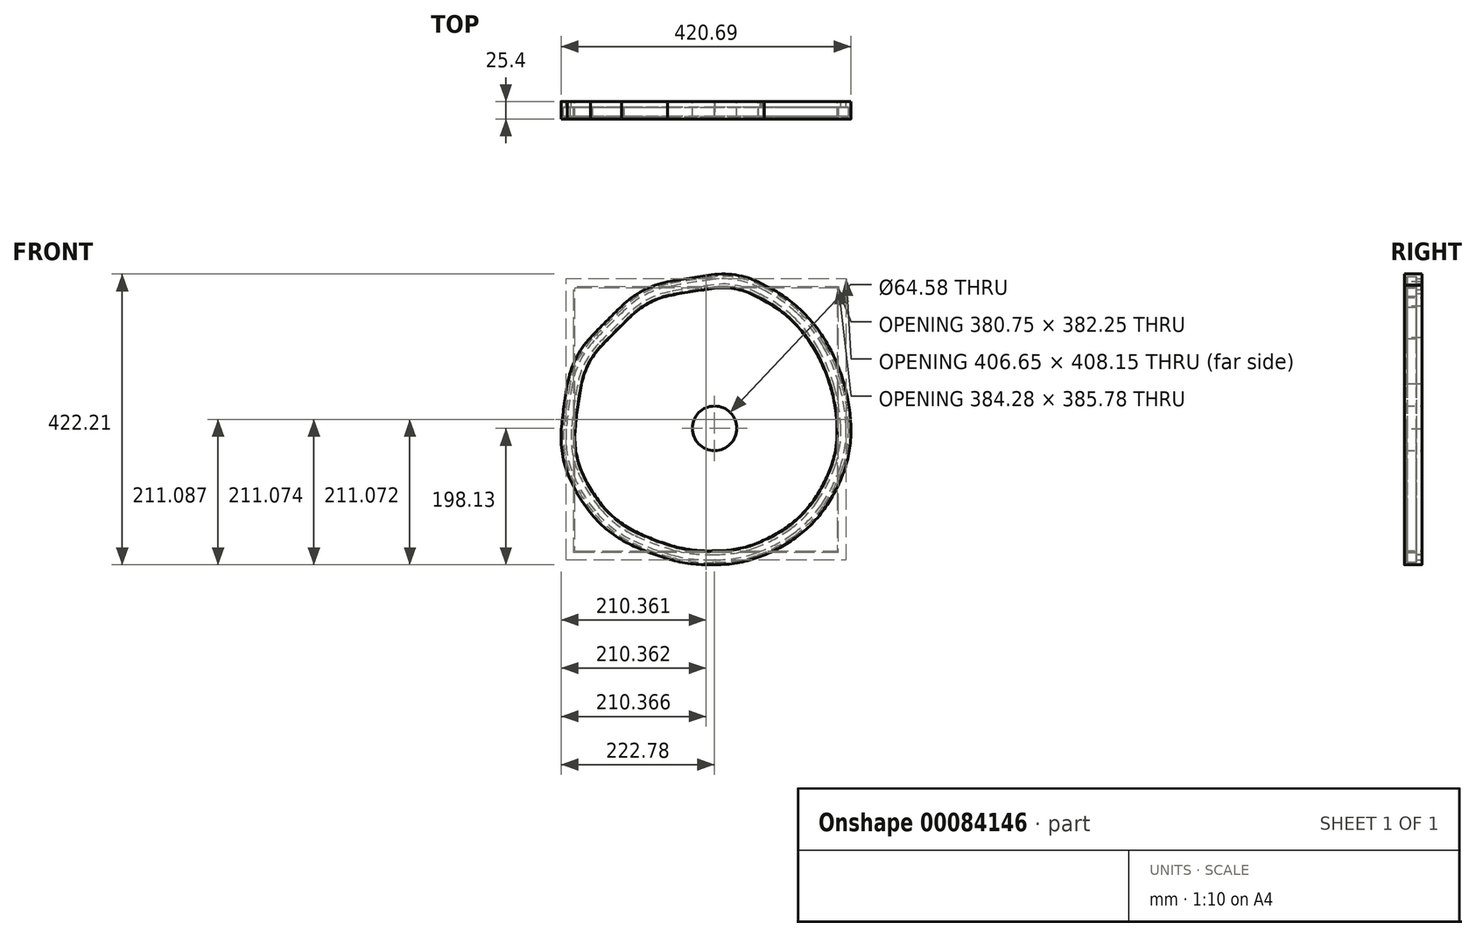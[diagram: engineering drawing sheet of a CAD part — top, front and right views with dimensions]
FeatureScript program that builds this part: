
annotation { "Feature Type Name" : "Feature", "Feature Type Description" : "" }
export const myFeature = defineFeature(function(context is Context, id is Id, definition is map)
    precondition{}
    {
        {
            var Q0;
            Q0=qCreatedBy(makeId("Front.planeOp"),FACE);
            var sketch = newSketch(context, id + "F0", { "sketchPlane" : qUnion([Q0])});
            skPoint(sketch, "E0", {"position": v(0, -177.8) * mm});
            skPoint(sketch, "E1", {"position": v(-58.17, -171.45) * mm});
            skPoint(sketch, "E2", {"position": v(-113.54, -150.62) * mm});
            skPoint(sketch, "E3", {"position": v(-161.3, -113.8) * mm});
            skPoint(sketch, "E4", {"position": v(-193.04, -61.72) * mm});
            skPoint(sketch, "E5", {"position": v(-202.18, -1.27) * mm});
            skPoint(sketch, "E6", {"position": v(-193.3, 62.74) * mm});
            skPoint(sketch, "E7", {"position": v(-164.34, 119.38) * mm});
            skPoint(sketch, "E8", {"position": v(-119.38, 164.34) * mm});
            skPoint(sketch, "E9", {"position": v(-62.74, 193.3) * mm});
            skPoint(sketch, "E10", {"position": v(0, 203.2) * mm});
            skArc(sketch, "E11", {"start": v(-58.17, -171.45) * mm, "mid": v(-29.35, -177.03) * mm, "end": v(0, -177.8) * mm});
            skArc(sketch, "E12", {"start": v(-113.54, -150.62) * mm, "mid": v(-86.3, -162.22) * mm, "end": v(-58.17, -171.45) * mm});
            skArc(sketch, "E13", {"start": v(-161.29, -113.8) * mm, "mid": v(-139.37, -134.74) * mm, "end": v(-113.54, -150.62) * mm});
            skArc(sketch, "E14", {"start": v(-193.04, -61.72) * mm, "mid": v(-179.18, -88.99) * mm, "end": v(-161.3, -113.8) * mm});
            skArc(sketch, "E15", {"start": v(-202.18, -1.27) * mm, "mid": v(-201.3, -32.05) * mm, "end": v(-193.04, -61.72) * mm});
            skArc(sketch, "E16", {"start": v(-193.3, 62.74) * mm, "mid": v(-198.47, 30.84) * mm, "end": v(-202.18, -1.27) * mm});
            skArc(sketch, "E17", {"start": v(-164.34, 119.38) * mm, "mid": v(-182.94, 93.17) * mm, "end": v(-193.3, 62.74) * mm});
            skArc(sketch, "E18", {"start": v(-119.38, 164.34) * mm, "mid": v(-142.13, 142.13) * mm, "end": v(-164.34, 119.38) * mm});
            skArc(sketch, "E19", {"start": v(-62.74, 193.3) * mm, "mid": v(-93.17, 182.94) * mm, "end": v(-119.38, 164.34) * mm});
            skArc(sketch, "E20", {"start": v(0, 203.2) * mm, "mid": v(-31.44, 198.67) * mm, "end": v(-62.74, 193.3) * mm});
            skPoint(sketch, "E21", {"position": v(63, 190) * mm});
            skPoint(sketch, "E22", {"position": v(111.5, 156.97) * mm});
            skPoint(sketch, "E23", {"position": v(147.07, 111) * mm});
            skPoint(sketch, "E24", {"position": v(168.91, 58.17) * mm});
            skPoint(sketch, "E25", {"position": v(177.8, 0) * mm});
            skPoint(sketch, "E26", {"position": v(169.16, -54.86) * mm});
            skPoint(sketch, "E27", {"position": v(143.76, -104.4) * mm});
            skPoint(sketch, "E28", {"position": v(104.4, -143.76) * mm});
            skPoint(sketch, "E29", {"position": v(54.86, -169.16) * mm});
            skArc(sketch, "E30", {"start": v(63, 190) * mm, "mid": v(32.62, 201.94) * mm, "end": v(0, 203.2) * mm});
            skArc(sketch, "E31", {"start": v(111.5, 156.97) * mm, "mid": v(88.62, 175.5) * mm, "end": v(63, 190) * mm});
            skArc(sketch, "E32", {"start": v(147.07, 111) * mm, "mid": v(131, 135.31) * mm, "end": v(111.5, 156.97) * mm});
            skArc(sketch, "E33", {"start": v(168.91, 58.17) * mm, "mid": v(159.54, 85.22) * mm, "end": v(147.07, 111) * mm});
            skArc(sketch, "E34", {"start": v(177.8, 0) * mm, "mid": v(175.15, 29.36) * mm, "end": v(168.9, 58.17) * mm});
            skArc(sketch, "E35", {"start": v(169.16, -54.86) * mm, "mid": v(176.02, -27.83) * mm, "end": v(177.8, 0) * mm});
            skArc(sketch, "E36", {"start": v(143.76, -104.4) * mm, "mid": v(158.11, -80.48) * mm, "end": v(169.16, -54.86) * mm});
            skArc(sketch, "E37", {"start": v(104.4, -143.76) * mm, "mid": v(125.84, -125.84) * mm, "end": v(143.76, -104.4) * mm});
            skArc(sketch, "E38", {"start": v(54.86, -169.16) * mm, "mid": v(80.48, -158.11) * mm, "end": v(104.4, -143.76) * mm});
            skArc(sketch, "E39", {"start": v(0, -177.8) * mm, "mid": v(27.83, -176.02) * mm, "end": v(54.86, -169.16) * mm});
            skCircle(sketch, "E40", {"center": v(0, 0) * mm, "radius": 32.3 * mm});
            skSolve(sketch);
        }
        {
            var Q0;
            Q0 = qSketchRegion(id + "F0", true);
            extrude(context, id + "F1", {"entities" : qUnion([Q0]), "depth" : 25.4 * mm});
        }
        {
            var Q0;
            Q0=makeQuery(id+"F1.opExtrude","CAP_FACE",FACE,{"disambiguationData":[OSD([sQuery(id+"F0.wireOp",EDGE,"E11"),sQuery(id+"F0.wireOp",EDGE,"E12"),sQuery(id+"F0.wireOp",EDGE,"E13"),sQuery(id+"F0.wireOp",EDGE,"E14"),sQuery(id+"F0.wireOp",EDGE,"E15"),sQuery(id+"F0.wireOp",EDGE,"E16"),sQuery(id+"F0.wireOp",EDGE,"E17"),sQuery(id+"F0.wireOp",EDGE,"E18"),sQuery(id+"F0.wireOp",EDGE,"E19"),sQuery(id+"F0.wireOp",EDGE,"E20"),sQuery(id+"F0.wireOp",EDGE,"E30"),sQuery(id+"F0.wireOp",EDGE,"E31"),sQuery(id+"F0.wireOp",EDGE,"E32"),sQuery(id+"F0.wireOp",EDGE,"E33"),sQuery(id+"F0.wireOp",EDGE,"E34"),sQuery(id+"F0.wireOp",EDGE,"E35"),sQuery(id+"F0.wireOp",EDGE,"E36"),sQuery(id+"F0.wireOp",EDGE,"E37"),sQuery(id+"F0.wireOp",EDGE,"E38"),sQuery(id+"F0.wireOp",EDGE,"E39"),sQuery(id+"F0.wireOp",EDGE,"E40")])],"isStart":true});
            var sketch = newSketch(context, id + "F2", { "sketchPlane" : qUnion([Q0])});
            skArc(sketch, "E41.0.0", {"start": v(58.17, -171.45) * mm, "mid": v(86.3, -162.22) * mm, "end": v(113.54, -150.62) * mm});
            skArc(sketch, "E41.0.1", {"start": v(113.54, -150.62) * mm, "mid": v(139.37, -134.74) * mm, "end": v(161.29, -113.8) * mm});
            skArc(sketch, "E41.0.2", {"start": v(161.3, -113.8) * mm, "mid": v(179.18, -88.99) * mm, "end": v(193.04, -61.72) * mm});
            skArc(sketch, "E41.0.3", {"start": v(193.04, -61.72) * mm, "mid": v(201.3, -32.05) * mm, "end": v(202.18, -1.27) * mm});
            skArc(sketch, "E41.0.4", {"start": v(202.18, -1.27) * mm, "mid": v(198.47, 30.84) * mm, "end": v(193.3, 62.74) * mm});
            skArc(sketch, "E41.0.5", {"start": v(193.3, 62.74) * mm, "mid": v(182.94, 93.17) * mm, "end": v(164.34, 119.38) * mm});
            skArc(sketch, "E41.0.6", {"start": v(164.34, 119.38) * mm, "mid": v(142.13, 142.13) * mm, "end": v(119.38, 164.34) * mm});
            skArc(sketch, "E41.0.7", {"start": v(119.38, 164.34) * mm, "mid": v(93.17, 182.94) * mm, "end": v(62.74, 193.3) * mm});
            skArc(sketch, "E41.0.8", {"start": v(62.74, 193.3) * mm, "mid": v(31.44, 198.67) * mm, "end": v(0, 203.2) * mm});
            skArc(sketch, "E41.0.9", {"start": v(0, 203.2) * mm, "mid": v(-32.62, 201.94) * mm, "end": v(-63, 190) * mm});
            skArc(sketch, "E41.0.10", {"start": v(-63, 190) * mm, "mid": v(-88.62, 175.5) * mm, "end": v(-111.5, 156.97) * mm});
            skArc(sketch, "E41.0.11", {"start": v(-111.5, 156.97) * mm, "mid": v(-131, 135.31) * mm, "end": v(-147.07, 111) * mm});
            skArc(sketch, "E41.0.12", {"start": v(-147.07, 111) * mm, "mid": v(-159.54, 85.22) * mm, "end": v(-168.91, 58.17) * mm});
            skArc(sketch, "E41.0.13", {"start": v(-168.9, 58.17) * mm, "mid": v(-175.15, 29.36) * mm, "end": v(-177.8, 0) * mm});
            skArc(sketch, "E41.0.14", {"start": v(-177.8, 0) * mm, "mid": v(-176.02, -27.83) * mm, "end": v(-169.16, -54.86) * mm});
            skArc(sketch, "E41.0.15", {"start": v(-169.16, -54.86) * mm, "mid": v(-158.11, -80.48) * mm, "end": v(-143.76, -104.4) * mm});
            skArc(sketch, "E41.0.16", {"start": v(-143.76, -104.4) * mm, "mid": v(-125.84, -125.84) * mm, "end": v(-104.4, -143.76) * mm});
            skArc(sketch, "E41.0.17", {"start": v(-104.4, -143.76) * mm, "mid": v(-80.48, -158.11) * mm, "end": v(-54.86, -169.16) * mm});
            skArc(sketch, "E41.0.18", {"start": v(-54.86, -169.16) * mm, "mid": v(-27.83, -176.02) * mm, "end": v(0, -177.8) * mm});
            skArc(sketch, "E41.0.19", {"start": v(0, -177.8) * mm, "mid": v(29.35, -177.03) * mm, "end": v(58.17, -171.45) * mm});
            skSolve(sketch);
        }
        {
            var Q0;
            Q0=qCreatedBy(makeId("Top.planeOp"),FACE);
            var sketch = newSketch(context, id + "F3", { "sketchPlane" : qUnion([Q0])});
            skLineSegment(sketch, "E42.0", {"start": v(-202.18, -25.4) * mm, "end": v(-202.18, 0) * mm});
            skLineSegment(sketch, "E43", {"start": v(-202.18, -25.4) * mm, "end": v(-222.2, -25.4) * mm});
            skLineSegment(sketch, "E44", {"start": v(-222.2, -25.4) * mm, "end": v(-222.2, -17.38) * mm});
            skLineSegment(sketch, "E45", {"start": v(-215.17, -21.57) * mm, "end": v(-203.96, -21.57) * mm});
            skLineSegment(sketch, "E46", {"start": v(-202.18, -12.7) * mm, "end": v(-227.74, -12.7) * mm, "construction": true});
            skPoint(sketch, "E46.endSnap0", {"position": v(-202.18, -12.7) * mm});
            skLineSegment(sketch, "E47.MirrorCS", {"start": v(-222.2, 0) * mm, "end": v(-222.2, -8.02) * mm});
            skLineSegment(sketch, "E48.MirrorCS", {"start": v(-218.68, -8.02) * mm, "end": v(-215.17, -8.02) * mm});
            skLineSegment(sketch, "E49.MirrorCS", {"start": v(-215.17, -8.02) * mm, "end": v(-215.17, -3.83) * mm});
            skLineSegment(sketch, "E50", {"start": v(-203.96, -21.57) * mm, "end": v(-203.96, -3.83) * mm});
            skLineSegment(sketch, "E51", {"start": v(-222.2, -8.02) * mm, "end": v(-222.2, -17.38) * mm});
            skLineSegment(sketch, "E52", {"start": v(-218.68, -8.02) * mm, "end": v(-218.68, -17.38) * mm});
            skPoint(sketch, "E53.MirrorCS.start.orphan", {"position": v(-202.18, 0) * mm});
            skLineSegment(sketch, "E54", {"start": v(-215.17, -3.83) * mm, "end": v(-215.17, 0) * mm});
            skLineSegment(sketch, "E55", {"start": v(-222.2, 0) * mm, "end": v(-215.17, 0) * mm});
            skPoint(sketch, "E55.endSnap0", {"position": v(-215.17, -0.7) * mm});
            skLineSegment(sketch, "E56", {"start": v(-202.18, 0) * mm, "end": v(-203.96, 0) * mm});
            skLineSegment(sketch, "E57", {"start": v(-203.96, -3.83) * mm, "end": v(-203.96, 0) * mm});
            skPoint(sketch, "E58.orphan", {"position": v(-215.17, 2.43) * mm});
            skLineSegment(sketch, "E59", {"start": v(-215.17, -21.57) * mm, "end": v(-218.68, -21.57) * mm});
            skLineSegment(sketch, "E60", {"start": v(-218.68, -17.38) * mm, "end": v(-218.68, -21.57) * mm});
            skPoint(sketch, "E61.start.orphan", {"position": v(-215.17, -17.38) * mm});
            skLineSegment(sketch, "E62", {"start": v(-207.46, -8.02) * mm, "end": v(-203.96, -8.02) * mm});
            skLineSegment(sketch, "E63", {"start": v(-203.96, 0) * mm, "end": v(-207.46, 0) * mm});
            skLineSegment(sketch, "E64", {"start": v(-207.46, 0) * mm, "end": v(-207.46, -8.02) * mm});
            skSolve(sketch);
        }
        {
            var Q0;
            Q0 = qSketchRegion(id + "F3", true);
            var Q1;
            Q1 = qConstructionFilter(qBodyType(qCreatedBy(id + "F2" ,EDGE), BodyType.WIRE), ConstructionObject.NO);
            sweep(context, id + "F4", {"profiles" : qUnion([Q0]), "path" : qUnion([Q1])});
        }
    });
